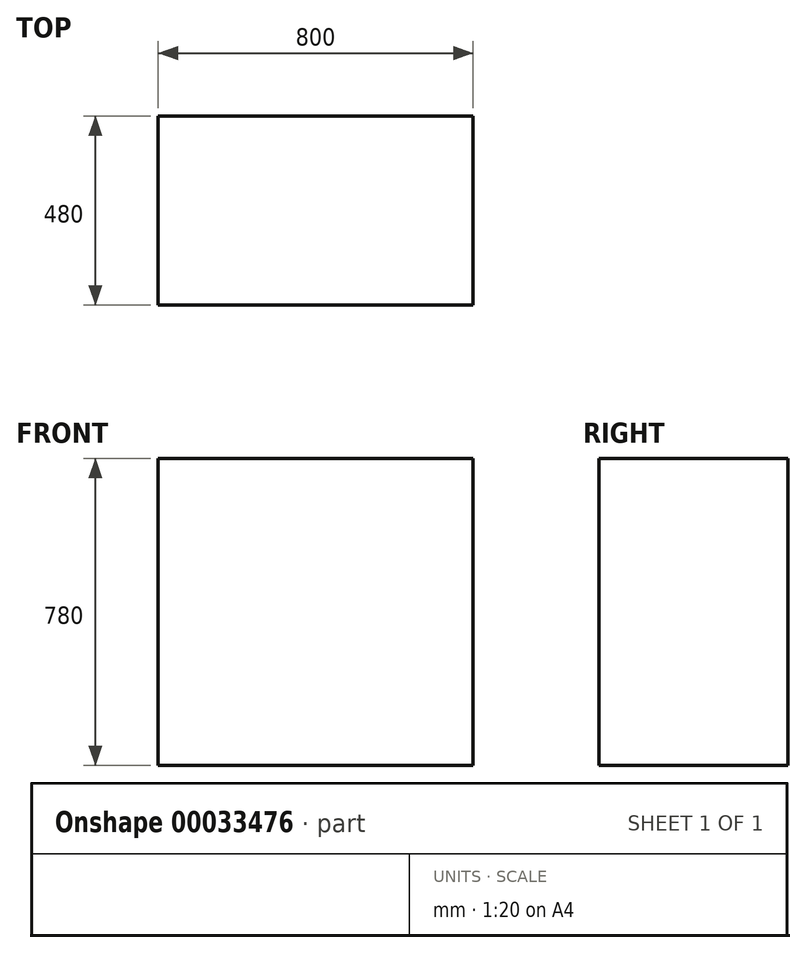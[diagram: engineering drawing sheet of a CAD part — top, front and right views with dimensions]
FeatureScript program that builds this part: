
annotation { "Feature Type Name" : "Feature", "Feature Type Description" : "" }
export const myFeature = defineFeature(function(context is Context, id is Id, definition is map)
    precondition{}
    {
        {
            var Q0;
            Q0=qCreatedBy(makeId("Top.planeOp"),FACE);
            var sketch = newSketch(context, id + "F0", { "sketchPlane" : qUnion([Q0])});
            skLineSegment(sketch, "E0.bottom", {"start": v(-402.05, 208.14) * mm, "end": v(397.95, 208.14) * mm});
            skLineSegment(sketch, "E0.top", {"start": v(-402.05, -271.86) * mm, "end": v(397.95, -271.86) * mm});
            skLineSegment(sketch, "E0.left", {"start": v(-402.05, 208.14) * mm, "end": v(-402.05, -271.86) * mm});
            skLineSegment(sketch, "E0.right", {"start": v(397.95, 208.14) * mm, "end": v(397.95, -271.86) * mm});
            skSolve(sketch);
        }
        {
            var Q0;
            Q0 = qSketchRegion(id + "F0", true);
            extrude(context, id + "F1", {"entities" : qUnion([Q0]), "depth" : 780 * mm});
        }
    });
